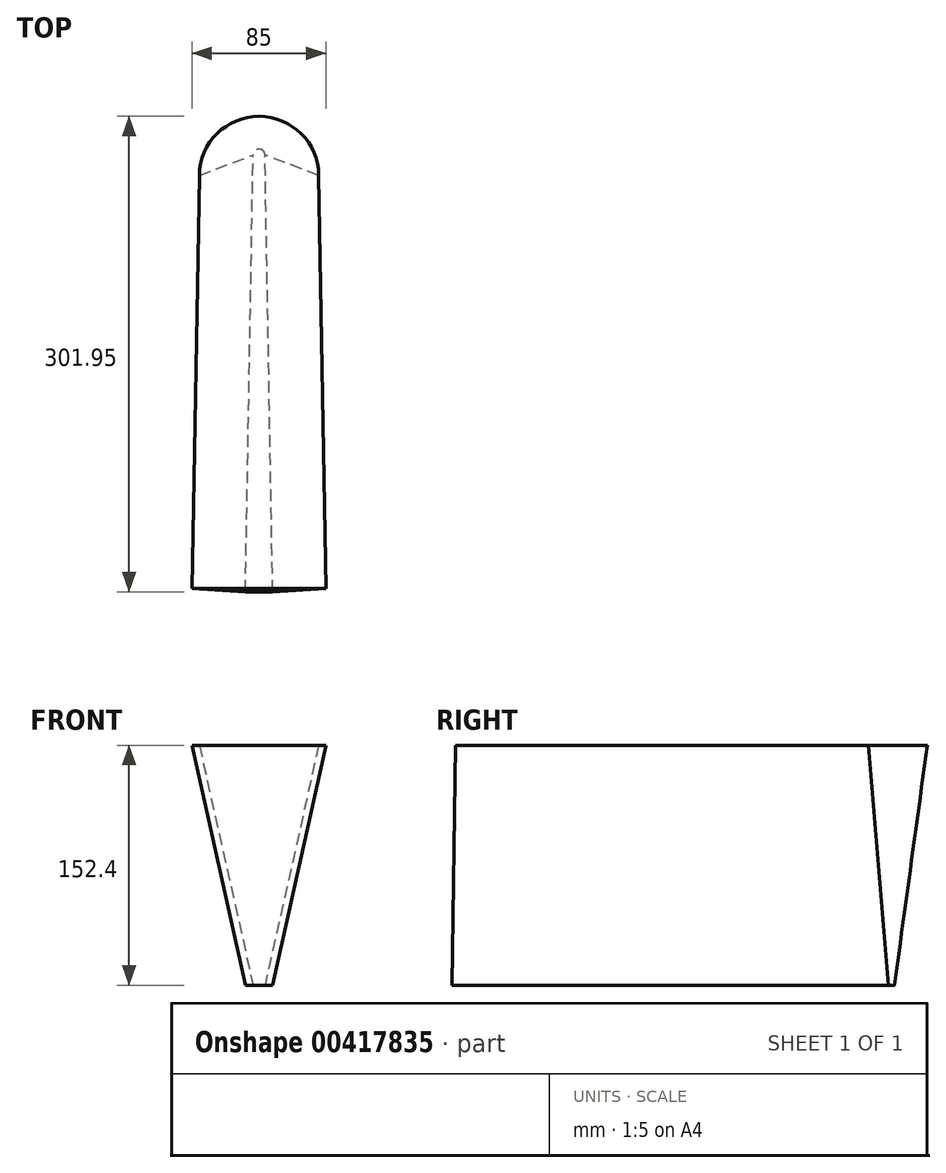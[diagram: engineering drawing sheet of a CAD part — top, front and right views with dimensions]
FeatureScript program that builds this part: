
annotation { "Feature Type Name" : "Feature", "Feature Type Description" : "" }
export const myFeature = defineFeature(function(context is Context, id is Id, definition is map)
    precondition{}
    {
        {
            var Q0;
            Q0=qCreatedBy(makeId("Top.planeOp"),FACE);
            cPlane(context, id + "F0", {"entities" : qUnion([Q0]), "cplaneType" : CPlaneType.OFFSET, "offset" : 152.4 * mm, "width" : 152.4 * mm, "height" : 152.4 * mm});
        }
        {
            var Q0;
            Q0=qCreatedBy(id+"F0.planeOp",FACE);
            var sketch = newSketch(context, id + "F1", { "sketchPlane" : qUnion([Q0])});
            skLineSegment(sketch, "E0", {"start": v(42.5, -194) * mm, "end": v(37.93, 68.3) * mm});
            skLineSegment(sketch, "E1", {"start": v(-42.5, -194) * mm, "end": v(-37.93, 68.3) * mm});
            skLineSegment(sketch, "E2", {"start": v(-42.5, -194) * mm, "end": v(42.5, -194) * mm});
            skArc(sketch, "E3", {"start": v(37.93, 68.3) * mm, "mid": v(0, 105.8) * mm, "end": v(-37.93, 68.3) * mm});
            skSolve(sketch);
        }
        {
            var Q0;
            Q0=qCreatedBy(makeId("Top.planeOp"),FACE);
            var sketch = newSketch(context, id + "F2", { "sketchPlane" : qUnion([Q0])});
            skLineSegment(sketch, "E4", {"start": v(-8.63, -196.14) * mm, "end": v(8.63, -196.14) * mm});
            skLineSegment(sketch, "E5", {"start": v(8.63, -196.14) * mm, "end": v(3.8, 81.2) * mm});
            skLineSegment(sketch, "E6", {"start": v(-8.63, -196.14) * mm, "end": v(-3.8, 81.2) * mm});
            skArc(sketch, "E7", {"start": v(3.8, 81.2) * mm, "mid": v(0, 84.98) * mm, "end": v(-3.8, 81.2) * mm});
            skSolve(sketch);
        }
        {
            var Q0;
            Q0 = qSketchRegion(id + "F1", true);
            var Q1;
            Q1 = qSketchRegion(id + "F2", true);
            loft(context, id + "F3", {"sheetProfilesArray" : [{ "sheetProfileEntities" : qUnion([Q0]) }, { "sheetProfileEntities" : qUnion([Q1]) }]});
        }
    });
